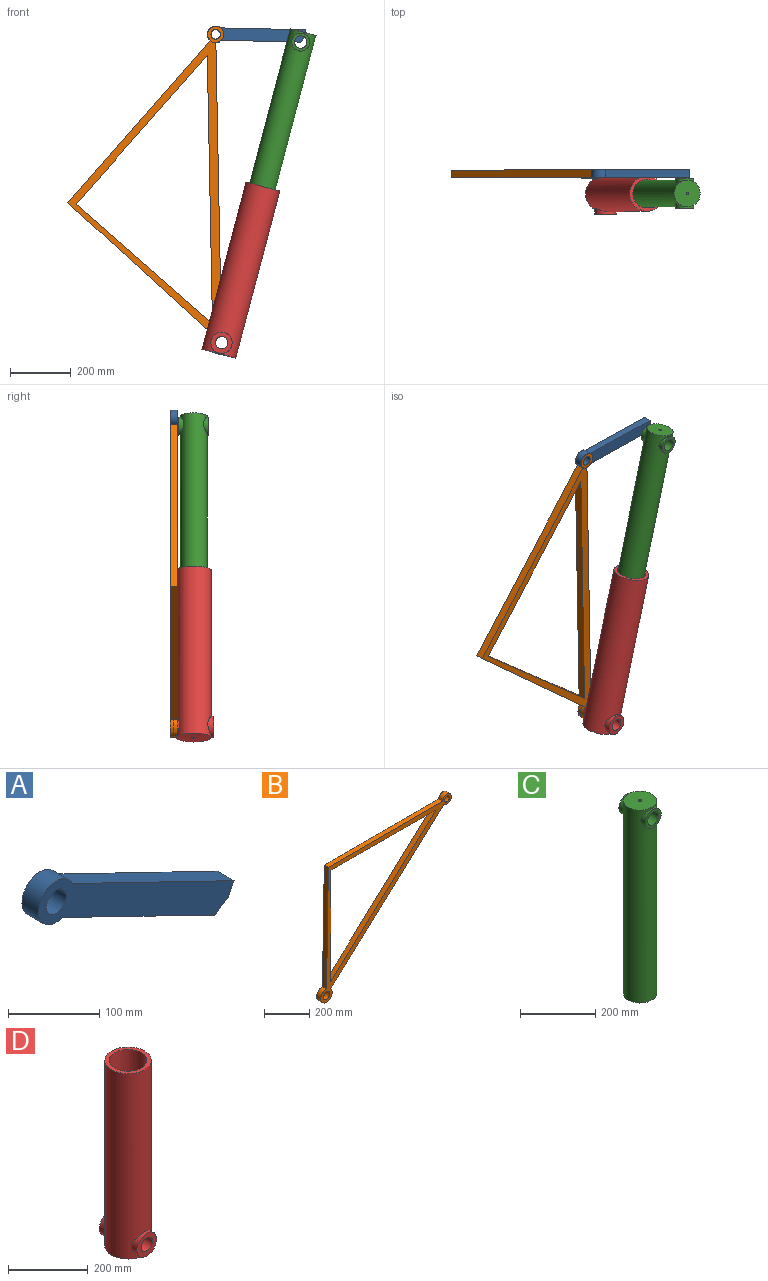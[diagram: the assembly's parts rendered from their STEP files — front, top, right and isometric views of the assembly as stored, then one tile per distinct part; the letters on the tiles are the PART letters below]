
ASSEMBLY  parts=4 mates=4
PART A: 8 faces, bbox 302.5x25.4x167.7 mm
  f0: plane 234.88x114.2mm, normal (-0.44,0,-0.9), area 6633.6mm2, adj f1,f5,f6,f7
  f1: plane 25.4x21.32mm, normal (0.5,0,-0.86), area 626.1mm2, adj f0,f2,f6,f7
  f2: plane 25.4x18.51mm, normal (0.9,0,-0.44), area 522.6mm2, adj f1,f3,f6,f7
  f3: plane 249.92x121.17mm, normal (0.44,0,0.9), area 7054.8mm2, adj f2,f5,f6,f7
  f4: cylinder r=15.42mm len=30.85mm, axis (0,1,0), area 2461.4mm2, adj f6,f7
  f5: cylinder r=27.65mm len=55.3mm, axis (0,1,0), area 3246.3mm2, adj f0,f3,f6,f7
  f6: plane 302.5x167.75mm, normal (0,-1,0), area 12555.8mm2, adj f0,f1,f2,f3,f4,f5
  f7: plane 302.5x167.75mm, normal (0,1,0), area 12555.8mm2, adj f0,f1,f2,f3,f4,f5
PART B: 12 faces, bbox 814.3x25.4x748.6 mm
  f0: cylinder r=26.71mm len=53.41mm, axis (0,1,0), area 3760.3mm2, adj f1,f9,f10,f11
  f1: plane 713.35x25.4mm, normal (0,0,1), area 18119.1mm2, adj f0,f2,f10,f11
  f2: plane 650.75x25.4mm, normal (-1,0,0.02), area 16531.6mm2, adj f1,f3,f10,f11
  f3: cylinder r=35.58mm len=71.15mm, axis (0,1,0), area 4942.5mm2, adj f2,f9,f10,f11
  f4: plane 654.65x25.4mm, normal (0,0,-1), area 16628.1mm2, adj f5,f6,f10,f11
  f5: plane 654.65x597.5mm, normal (-0.67,0,0.74), area 22512.5mm2, adj f4,f6,f10,f11
  f6: plane 599.13x25.4mm, normal (1,0,0), area 15217.8mm2, adj f4,f5,f10,f11
  f7: cylinder r=15.58mm len=31.16mm, axis (0,1,0), area 2486.5mm2, adj f10,f11
  f8: cylinder r=20.67mm len=41.33mm, axis (0,1,0), area 3298.3mm2, adj f10,f11
  f9: plane 706.01x644.38mm, normal (0.67,0,-0.74), area 24278.9mm2, adj f0,f3,f10,f11
  f10: plane 814.3x748.64mm, normal (0,-1,0), area 61183.5mm2, adj f0,f1,f2,f3,f4,f5,f6,f7
  f11: plane 814.3x748.64mm, normal (0,1,0), area 61183.5mm2, adj f0,f1,f2,f3,f4,f5,f6,f7
PART C: 12 faces, bbox 88.2x98.9x627.4 mm
  f0: cylinder r=4.24mm len=8.47mm, axis (0,0,-1), area 106mm2, adj f4,f10
  f1: cylinder r=4.24mm len=564.51mm, axis (0,0,-1), area 15019.2mm2, adj f3,f9
  f2: cylinder r=44.09mm len=627.39mm, axis (0,0,-1), area 167878.6mm2, adj f3,f4,f6,f8
  f3: plane 88.17x88.17mm, normal (0,0,-1), area 6049.7mm2, adj f1,f2
  f4: plane 88.17x88.17mm, normal (0,0,1), area 6049.7mm2, adj f0,f2
  f5: plane 59.36x59.36mm, normal (0,1,0), area 1449.2mm2, adj f6,f11
  f6: cylinder r=29.68mm len=59.36mm, axis (0,1,0), area 2030.6mm2, adj f2,f5
  f7: plane 59.36x59.36mm, normal (0,-1,0), area 1449.2mm2, adj f8,f11
  f8: cylinder r=29.68mm len=59.36mm, axis (0,1,0), area 2031.6mm2, adj f2,f7
  f9: cylinder r=29.68mm len=8.47mm, axis (0,1,0), area 56.5mm2, adj f1
  f10: cylinder r=29.68mm len=8.47mm, axis (0,1,0), area 56.5mm2, adj f0
  f11: cylinder r=20.48mm len=98.91mm, axis (0,-1,0), area 12729.3mm2, adj f5,f7
PART D: 14 faces, bbox 116.7x133.5x571.5 mm
  f0: cylinder r=58.33mm len=569.79mm, axis (0,0,1), area 200771.7mm2, adj f3,f6,f10,f11
  f1: cone r=4.04mm half-angle=2.1deg, axis (0,0,-1), area 154.2mm2, adj f6,f8
  f2: cone r=4.04mm half-angle=2.1deg, axis (0,0,-1), area 17.6mm2, adj f5,f7
  f3: plane 116.67x116.67mm, normal (0,0,1), area 3738.7mm2, adj f0,f4
  f4: cylinder r=47.04mm len=497.73mm, axis (0,0,1), area 147109.6mm2, adj f3,f5
  f5: cone r=47.04mm half-angle=89.9deg, axis (0,0,1), area 6900.3mm2, adj f2,f4
  f6: cone r=6.74mm half-angle=88.1deg, axis (0,0,1), area 10553.4mm2, adj f0,f1
  f7: cylinder r=34.9mm len=8.14mm, axis (0,1,0), area 51.9mm2, adj f2
  f8: cylinder r=34.9mm len=13.23mm, axis (0,1,0), area 137.6mm2, adj f1
  f9: plane 69.8x69.8mm, normal (0,1,0), area 2560.2mm2, adj f10,f13
  f10: cylinder r=34.9mm len=69.8mm, axis (0,1,0), area 3078.3mm2, adj f0,f9
  f11: cylinder r=34.9mm len=69.8mm, axis (0,1,0), area 3077.8mm2, adj f0,f12
  f12: plane 69.8x69.8mm, normal (0,-1,0), area 2560.2mm2, adj f11,f13
  f13: cylinder r=20.07mm len=133.47mm, axis (0,1,0), area 16833.7mm2, adj f9,f12
PLACE A rot(axis=(0,-1,0),24.6deg) t=(1538.84,-644.11,-148.31)mm
PLACE B rot(axis=(0,-1,0),48.7deg) t=(1726.66,-644.11,394.19)mm
PLACE C rot(axis=(0,1,0),14.7deg) t=(505.99,-722.14,17.08)mm
PLACE D rot(axis=(0,1,0),14.7deg) t=(517.3,-722.14,60.08)mm
MATE cylindrical D.f13 <-> B.f3  axis (0,1,0) through (381.77,-655.41,-455.08)mm
MATE revolute A.f4 <-> B.f0  axis (0,-1,0) through (362.19,-669.51,562.88)mm
MATE cylindrical A.f6 <-> C.f6  axis (0,1,0) through (642.87,-669.51,537.37)mm
MATE cylindrical C.f0 <-> D.f0  axis (-0.25,0,-0.97) through (571.58,-722.14,266.4)mm
